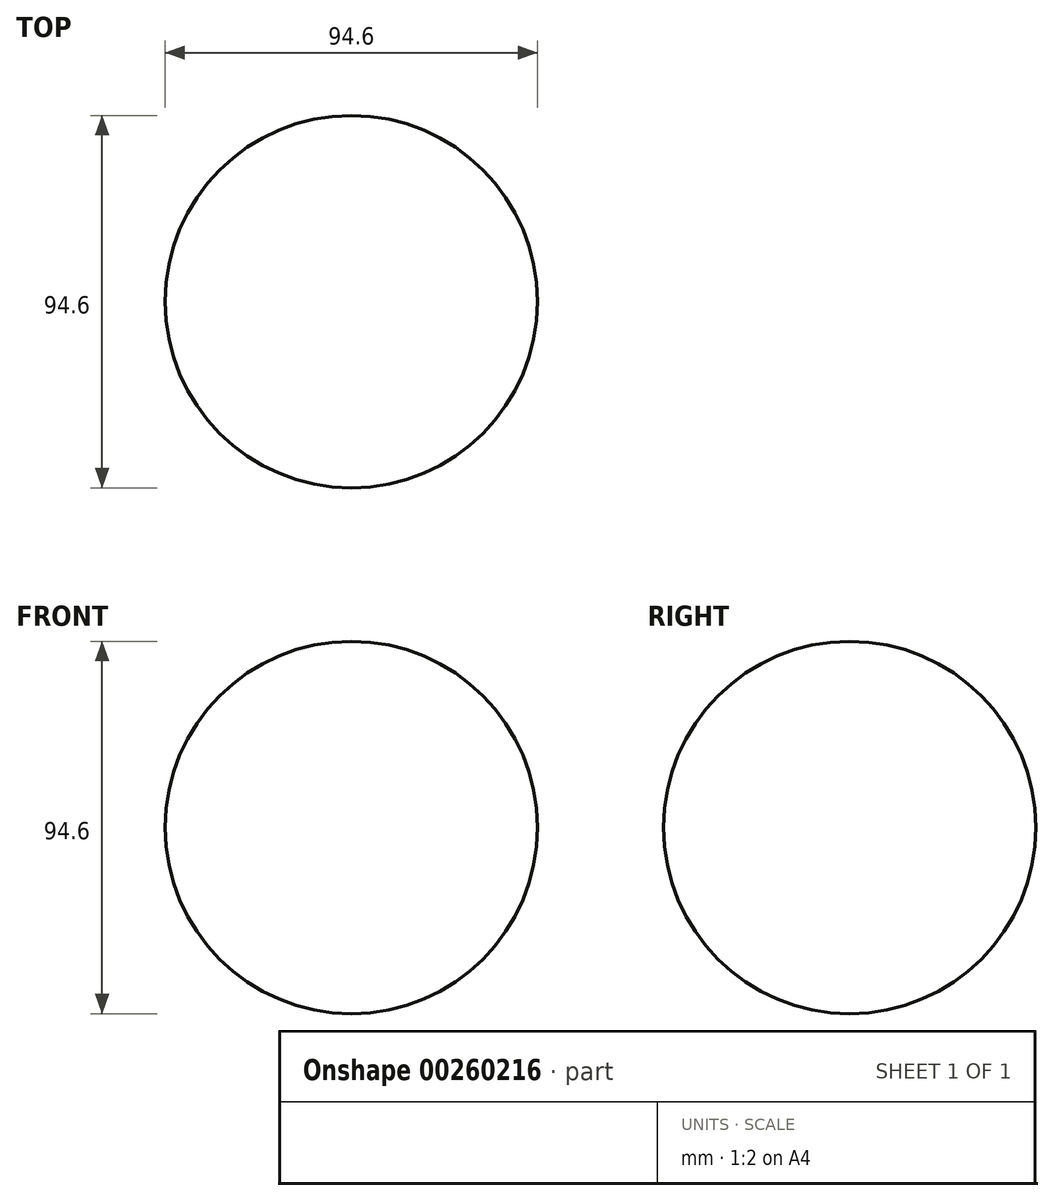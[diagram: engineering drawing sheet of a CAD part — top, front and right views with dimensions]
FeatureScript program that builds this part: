
annotation { "Feature Type Name" : "Feature", "Feature Type Description" : "" }
export const myFeature = defineFeature(function(context is Context, id is Id, definition is map)
    precondition{}
    {
        {
            var Q0;
            Q0=qCreatedBy(makeId("Front.planeOp"),FACE);
            var sketch = newSketch(context, id + "F0", { "sketchPlane" : qUnion([Q0])});
            skArc(sketch, "E0", {"start": v(0, 47.3) * mm, "mid": v(-47.3, 0) * mm, "end": v(0, -47.3) * mm});
            skLineSegment(sketch, "E1", {"start": v(0, 68.95) * mm, "end": v(0, -78.13) * mm, "construction": true});
            skLineSegment(sketch, "E2", {"start": v(-77.42, 0) * mm, "end": v(74.13, 0) * mm, "construction": true});
            skLineSegment(sketch, "E3", {"start": v(0, 47.3) * mm, "end": v(0, -47.3) * mm});
            skSolve(sketch);
        }
        {
            var Q0;
            Q0=makeQuery(id+"F0.imprint","IMPRINT",FACE,{"disambiguationData":[TD([[makeQuery(id+"F0.imprint","IMPRINT",EDGE,{"derivedFrom":sQuery(id+"F0.wireOp",EDGE,"E0")}),1.0]])]});
            var Q1;
            Q1 = qConstructionFilter(qBodyType(qCreatedBy(id + "F0" ,EDGE), BodyType.WIRE), ConstructionObject.NO);
            var Q2;
            Q2=sQuery(id+"F0.wireOp",EDGE,"E1");
            revolve(context, id + "F1", {"entities" : qUnion([Q0]), "surfaceEntities" : qUnion([Q1]), "axis" : qUnion([Q2]), "revolveType" : RevolveType.FULL});
        }
        {
            var Q0;
            Q0=qCreatedBy(makeId("Front.planeOp"),FACE);
            cPlane(context, id + "F2", {"entities" : qUnion([Q0]), "cplaneType" : CPlaneType.OFFSET, "offset" : 25.4 * mm, "width" : 152.4 * mm, "height" : 152.4 * mm});
        }
    });
